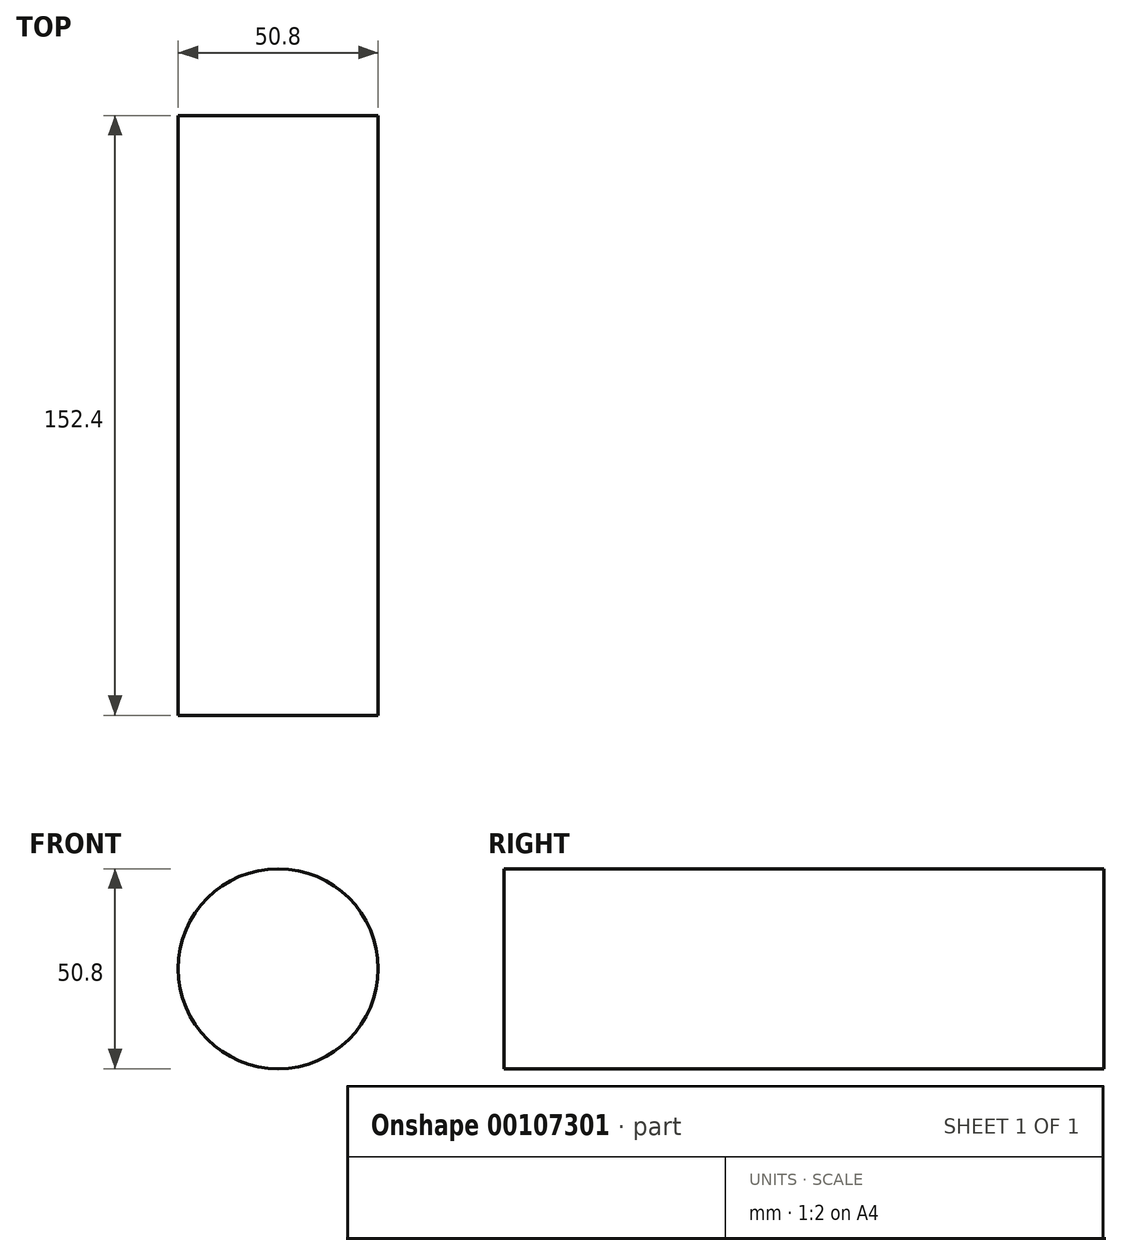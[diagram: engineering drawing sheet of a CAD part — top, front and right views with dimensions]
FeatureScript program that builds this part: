
annotation { "Feature Type Name" : "Feature", "Feature Type Description" : "" }
export const myFeature = defineFeature(function(context is Context, id is Id, definition is map)
    precondition{}
    {
        {
            var Q0;
            Q0=qCreatedBy(makeId("Front.planeOp"),FACE);
            var sketch = newSketch(context, id + "F0", { "sketchPlane" : qUnion([Q0])});
            skCircle(sketch, "E0", {"center": v(-42.87, 38.8) * mm, "radius": 25.4 * mm});
            skSolve(sketch);
        }
        {
            var Q0;
            Q0=makeQuery(id+"F0.imprint","IMPRINT",FACE,{"disambiguationData":[TD([[makeQuery(id+"F0.imprint","IMPRINT",EDGE,{"derivedFrom":sQuery(id+"F0.wireOp",EDGE,"E0")}),1.0]])]});
            extrude(context, id + "F1", {"entities" : qUnion([Q0]), "depth" : 76.2 * mm, "hasSecondDirection" : true, "secondDirectionOppositeDirection" : true, "secondDirectionDepth" : 76.2 * mm});
        }
    });
